# Revit family: FP-Revit20-en-CG301DNGGB4-GasOnGlassCooktop-0-90004462A-CN
name_source: partatom
category: Specialty Equipment
units: mm (PartAtom-declared; Revit-internal decimal feet)

## family parameters
Always vertical = Yes
Cut with Voids When Loaded = Yes
OmniClass Number = 23.40.40.14.17.11
OmniClass Title = Cookers, Ovens, Stoves
Part Type = Normal
Room Calculation Point = No
Round Connector Dimension = Use Diameter
Shared = No
Work Plane-Based = No

## types (1)
- JZT-CG301DNGGB4
    Cavity - Depth = 490 mm  [stored 1.60761 ft]
    Cavity - Height = 59 mm
    Cavity - Width = 260 mm  [stored 0.853018 ft]
    Chassis - Depth = 486 mm  [stored 1.59449 ft]
    Chassis - Height = 59 mm
    Chassis - Width = 256 mm  [stored 0.839895 ft]
    Clearance - Below Combustible = 70 mm  [stored 0.229659 ft]
    Clearance - Below Non-Combustible = 65 mm  [stored 0.213255 ft]
    Clearance - Overhead Combustible = 650 mm  [stored 2.13255 ft]
    Clearance - Overhead Non-Combustible = 500 mm  [stored 1.64042 ft]
    Clearance - Overhead Rangehood = 650 mm  [stored 2.13255 ft]
    Clearance - Rear Combustible = 160 mm  [stored 0.524934 ft]
    Clearance - Rear Non-Combustible = 45 mm  [stored 0.147638 ft]
    Clearance - Side Combustible = 120 mm  [stored 0.393701 ft]
    Connector Note - Electrical = 230 V, 10 A, fused electrical supply
    Connector Note - Gas = NG 1 kPa (4" WC), Connection is Rp 1/2" (ISO7-1)
    Default Elevation = 0 mm  [stored 0 ft]
    Description = 30cm Series 9 1 Burner Gas Cooktop, Natural Gas
    Manufacturer = Fisher & Paykel Appliances
    Material - Body = Fisher & Paykel - Grey
    Material - Burners & Trivets = Fisher & Paykel - Black, Matte
    Material - Cooktop = Fisher & Paykel - Glass, Black
    Material - Trim = Fisher & Paykel - Aluminium, Dark
    Model = JZT-CG301DNGGB4
    Product - Depth = 530 mm  [stored 1.73885 ft]
    Product - Height = 125 mm  [stored 0.410105 ft]
    Product - Width = 300 mm  [stored 0.984252 ft]
    URL = www.fisherpaykel.com
    Visibility - Clearance Required = Yes

note: [stored X ft] marks values corroborated as IEEE doubles in the binary element streams (Revit-internal decimal feet)

## geometry (parser evidence)
native form markers: Sweep x10
no freeform markers — native parametric forms only
